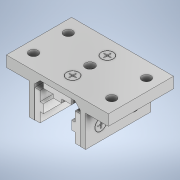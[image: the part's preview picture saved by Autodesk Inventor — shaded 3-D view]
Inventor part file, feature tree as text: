
AUTODESK INVENTOR PART (.ipt)
format: ipt  version: 2020 (Build 240168000, 168)  size: 244,736 bytes
history: native  units: mm
features: other x3, mirror x1
ambient origin geometry x8: Origin, YZ Plane, XZ Plane, XY Plane, X Axis, Y Axis, Z Axis, Center Point
bodies: Solid1 (feature_tree), Solid2 (feature_tree), Solid3 (feature_tree), Solid4 (feature_tree)
feature tree (4):
  mirror  "Mirror1"
  other  "Cut-Extrude5"
  other  "Cut-Extrude6"
  other  "Top Flange Hole"
